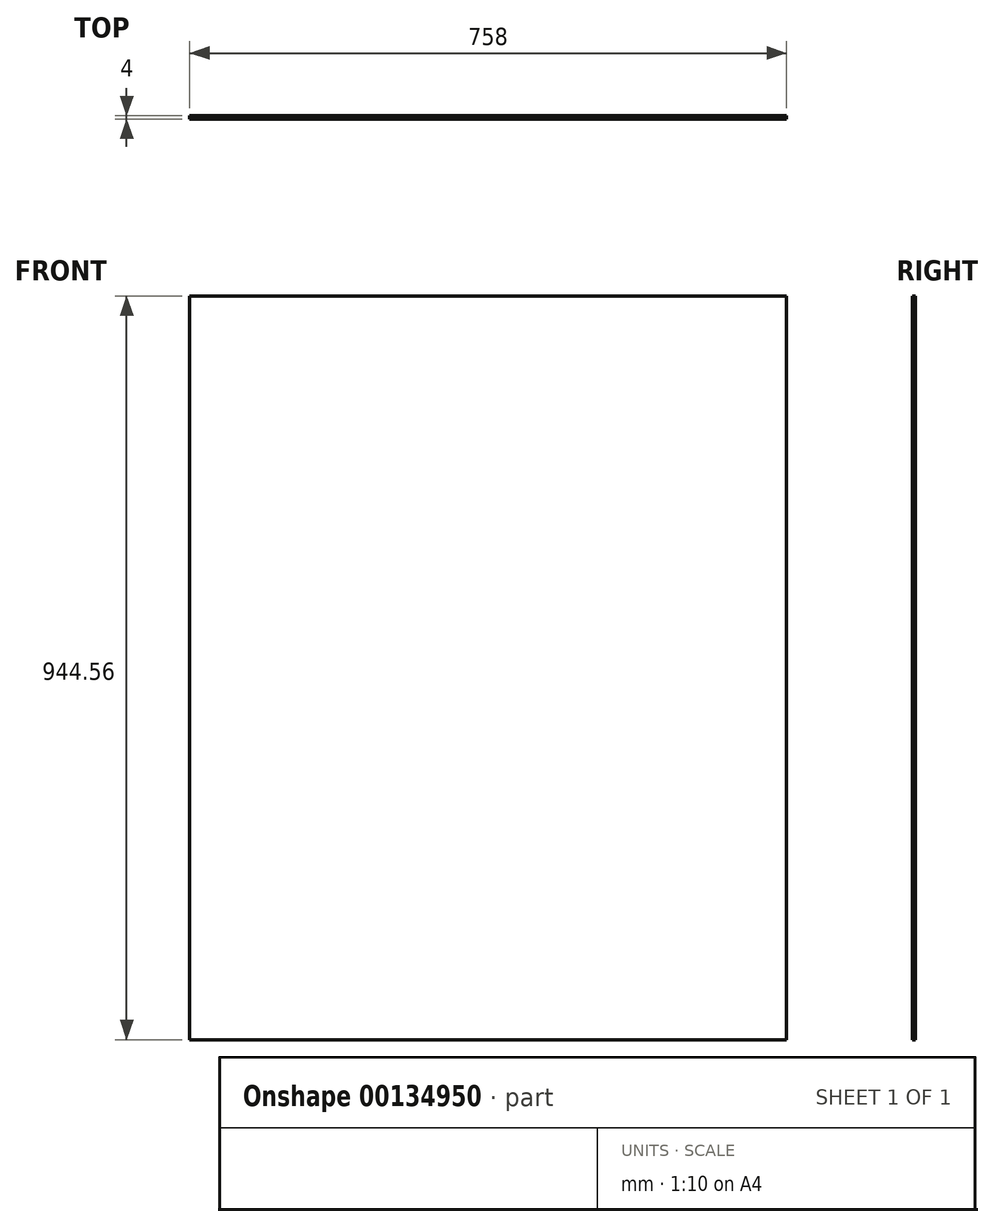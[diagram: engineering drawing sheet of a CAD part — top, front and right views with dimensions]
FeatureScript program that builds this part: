
annotation { "Feature Type Name" : "Feature", "Feature Type Description" : "" }
export const myFeature = defineFeature(function(context is Context, id is Id, definition is map)
    precondition{}
    {
        {
            var Q0;
            Q0=qCreatedBy(makeId("Front.planeOp"),FACE);
            var sketch = newSketch(context, id + "F0", { "sketchPlane" : qUnion([Q0])});
            skLineSegment(sketch, "E0.bottom", {"start": v(0, 0) * mm, "end": v(758, 0) * mm});
            skLineSegment(sketch, "E0.top", {"start": v(0, 944.56) * mm, "end": v(758, 944.56) * mm});
            skLineSegment(sketch, "E0.left", {"start": v(0, 0) * mm, "end": v(0, 944.56) * mm});
            skLineSegment(sketch, "E0.right", {"start": v(758, 0) * mm, "end": v(758, 944.56) * mm});
            skSolve(sketch);
        }
        {
            var Q0;
            Q0=makeQuery(id+"F0.imprint","IMPRINT",FACE,{"disambiguationData":[TD([[makeQuery(id+"F0.imprint","IMPRINT",EDGE,{"derivedFrom":sQuery(id+"F0.wireOp",EDGE,"E0.bottom")}),1.0]])]});
            extrude(context, id + "F1", {"entities" : qUnion([Q0]), "depth" : 4 * mm});
        }
    });
